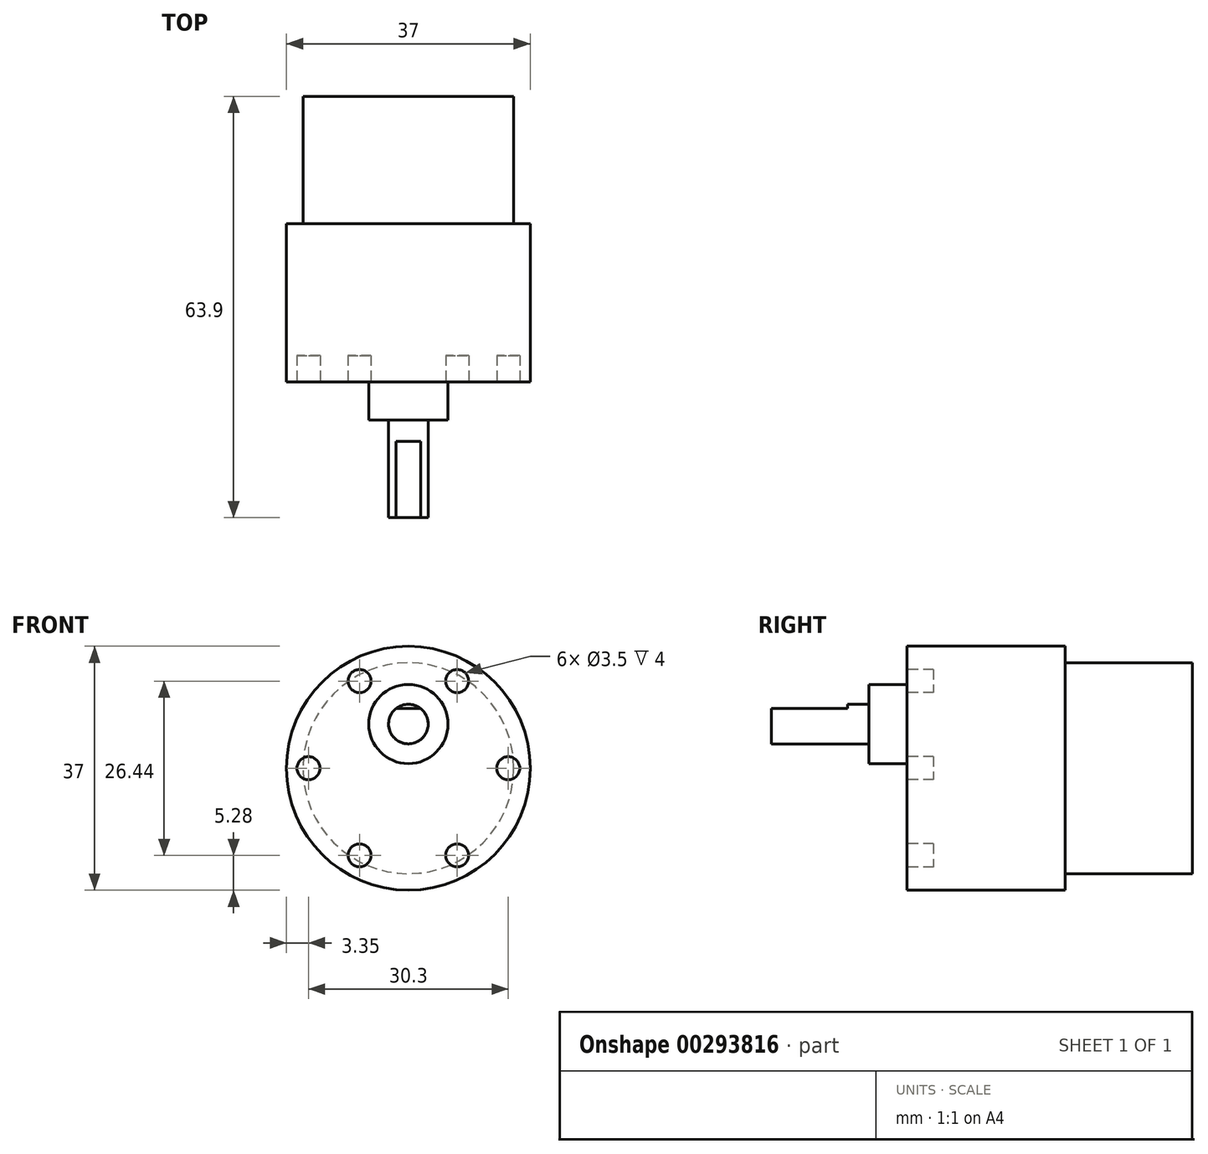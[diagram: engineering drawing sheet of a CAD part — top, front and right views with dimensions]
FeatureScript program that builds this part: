
annotation { "Feature Type Name" : "Feature", "Feature Type Description" : "" }
export const myFeature = defineFeature(function(context is Context, id is Id, definition is map)
    precondition{}
    {
        {
            var Q0;
            Q0=qCreatedBy(makeId("Front.planeOp"),FACE);
            var sketch = newSketch(context, id + "F0", { "sketchPlane" : qUnion([Q0])});
            skArc(sketch, "E0", {"start": v(-1.86, 2.35) * mm, "mid": v(0, -3) * mm, "end": v(1.86, 2.35) * mm});
            skLineSegment(sketch, "E1", {"start": v(-1.86, 2.35) * mm, "end": v(1.86, 2.35) * mm});
            skSolve(sketch);
        }
        {
            var Q0;
            Q0 = qSketchRegion(id + "F0", true);
            extrude(context, id + "F1", {"entities" : qUnion([Q0]), "oppositeDirection" : true, "depth" : 11.6 * mm});
        }
        {
            var Q0;
            Q0=makeQuery(id+"F1.opExtrude","CAP_FACE",FACE,{"disambiguationData":[OSD([sQuery(id+"F0.wireOp",EDGE,"E0"),sQuery(id+"F0.wireOp",EDGE,"E1")])],"isStart":false});
            cPlane(context, id + "F2", {"entities" : qUnion([Q0]), "cplaneType" : CPlaneType.OFFSET, "offset" : 0 * mm, "width" : 150 * mm, "height" : 150 * mm});
        }
        {
            var Q0;
            Q0=qCreatedBy(id+"F2.planeOp",FACE);
            var sketch = newSketch(context, id + "F3", { "sketchPlane" : qUnion([Q0])});
            skCircle(sketch, "E2", {"center": v(0, 0) * mm, "radius": 3 * mm});
            skSolve(sketch);
        }
        {
            var Q0;
            Q0 = qSketchRegion(id + "F3", true);
            extrude(context, id + "F4", {"entities" : qUnion([Q0]), "operationType" : NewBodyOperationType.ADD, "depth" : 3.2 * mm});
        }
        {
            var Q0;
            Q0=makeQuery(id+"F4.opExtrude","CAP_FACE",FACE,{"disambiguationData":[OSD([sQuery(id+"F3.wireOp",EDGE,"E2")])],"isStart":false});
            cPlane(context, id + "F5", {"entities" : qUnion([Q0]), "cplaneType" : CPlaneType.OFFSET, "offset" : 0 * mm, "width" : 150 * mm, "height" : 150 * mm});
        }
        {
            var Q0;
            Q0=qCreatedBy(id+"F5.planeOp",FACE);
            var sketch = newSketch(context, id + "F6", { "sketchPlane" : qUnion([Q0])});
            skCircle(sketch, "E3", {"center": v(0, 0) * mm, "radius": 6 * mm});
            skSolve(sketch);
        }
        {
            var Q0;
            Q0 = qSketchRegion(id + "F6", true);
            extrude(context, id + "F7", {"entities" : qUnion([Q0]), "operationType" : NewBodyOperationType.ADD, "depth" : 5.8 * mm});
        }
        {
            var Q0;
            Q0=makeQuery(id+"F7.opExtrude","CAP_FACE",FACE,{"disambiguationData":[OSD([sQuery(id+"F6.wireOp",EDGE,"E3")])],"isStart":false});
            cPlane(context, id + "F8", {"entities" : qUnion([Q0]), "cplaneType" : CPlaneType.OFFSET, "offset" : 0 * mm, "width" : 150 * mm, "height" : 150 * mm});
        }
        {
            var Q0;
            Q0=qCreatedBy(id+"F8.planeOp",FACE);
            var sketch = newSketch(context, id + "F9", { "sketchPlane" : qUnion([Q0])});
            skCircle(sketch, "E4", {"center": v(0, -6.7) * mm, "radius": 18.5 * mm});
            skSolve(sketch);
        }
        {
            var Q0;
            Q0 = qSketchRegion(id + "F9", true);
            extrude(context, id + "F10", {"entities" : qUnion([Q0]), "operationType" : NewBodyOperationType.ADD, "depth" : 24 * mm});
        }
        {
            var Q0;
            Q0=makeQuery(id+"F10.opExtrude","CAP_FACE",FACE,{"disambiguationData":[OSD([sQuery(id+"F9.wireOp",EDGE,"E4")])],"isStart":false});
            cPlane(context, id + "F11", {"entities" : qUnion([Q0]), "cplaneType" : CPlaneType.OFFSET, "offset" : 0 * mm, "width" : 150 * mm, "height" : 150 * mm});
        }
        {
            var Q0;
            Q0=qCreatedBy(id+"F11.planeOp",FACE);
            var sketch = newSketch(context, id + "F12", { "sketchPlane" : qUnion([Q0])});
            skCircle(sketch, "E5.0", {"center": v(0, -6.7) * mm, "radius": 18.5 * mm, "construction": true});
            skCircle(sketch, "E6", {"center": v(0, -6.7) * mm, "radius": 16 * mm});
            skSolve(sketch);
        }
        {
            var Q0;
            Q0 = qSketchRegion(id + "F12", true);
            extrude(context, id + "F13", {"entities" : qUnion([Q0]), "operationType" : NewBodyOperationType.ADD, "depth" : 19.3 * mm});
        }
        {
            var Q0;
            Q0=qCreatedBy(id+"F8.planeOp",FACE);
            var sketch = newSketch(context, id + "F14", { "sketchPlane" : qUnion([Q0])});
            skCircle(sketch, "E7.0", {"center": v(0, -6.7) * mm, "radius": 18.5 * mm, "construction": true});
            skCircle(sketch, "E8", {"center": v(0, -6.7) * mm, "radius": 15.15 * mm, "construction": true});
            skCircle(sketch, "E9", {"center": v(-15.15, -6.7) * mm, "radius": 1.75 * mm});
            skCircle(sketch, "E10", {"center": v(15.15, -6.7) * mm, "radius": 1.75 * mm});
            skCircle(sketch, "E11", {"center": v(7.4, -19.92) * mm, "radius": 1.75 * mm});
            skCircle(sketch, "E12", {"center": v(-7.4, -19.92) * mm, "radius": 1.75 * mm});
            skLineSegment(sketch, "E13", {"start": v(7.4, -19.92) * mm, "end": v(-7.4, 6.52) * mm, "construction": true});
            skCircle(sketch, "E14", {"center": v(-7.4, 6.52) * mm, "radius": 1.75 * mm});
            skLineSegment(sketch, "E15", {"start": v(-7.4, -19.92) * mm, "end": v(7.4, 6.52) * mm, "construction": true});
            skCircle(sketch, "E16", {"center": v(7.4, 6.52) * mm, "radius": 1.75 * mm});
            skSolve(sketch);
        }
        {
            var Q0;
            Q0 = qSketchRegion(id + "F14", true);
            extrude(context, id + "F15", {"entities" : qUnion([Q0]), "operationType" : NewBodyOperationType.REMOVE, "depth" : 4 * mm});
        }
    });
